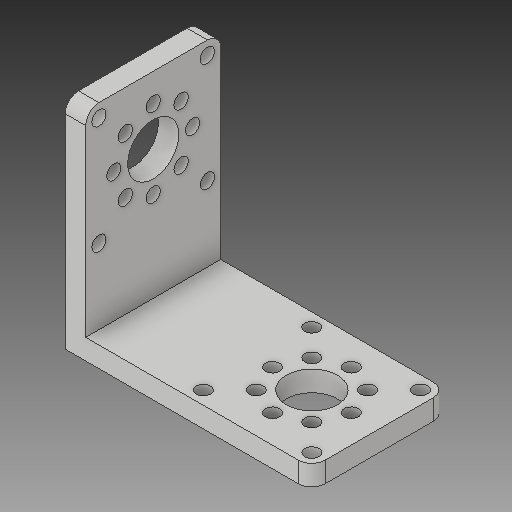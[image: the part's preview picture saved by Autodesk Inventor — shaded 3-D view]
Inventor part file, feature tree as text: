
AUTODESK INVENTOR PART (.ipt)
format: ipt  version: 2017 (Build 210142000, 142)  size: 171,520 bytes
history: native  units: in
note: dims shown in document units (in); Inventor stores cm internally (conversion verified against a paired STEP export)
features: fillet x1
ambient origin geometry x8: Origin, YZ Plane, XZ Plane, XY Plane, X Axis, Y Axis, Z Axis, Center Point
bodies: Solid1 (feature_tree)
feature tree (1):
  fillet  "Fillet1"  [1 undecoded]
note: 1 required parameter value undecoded (feature->parameter linkage not recoverable at this tier; creation-order binding heuristic only, values carry confidence <= 0.55)
